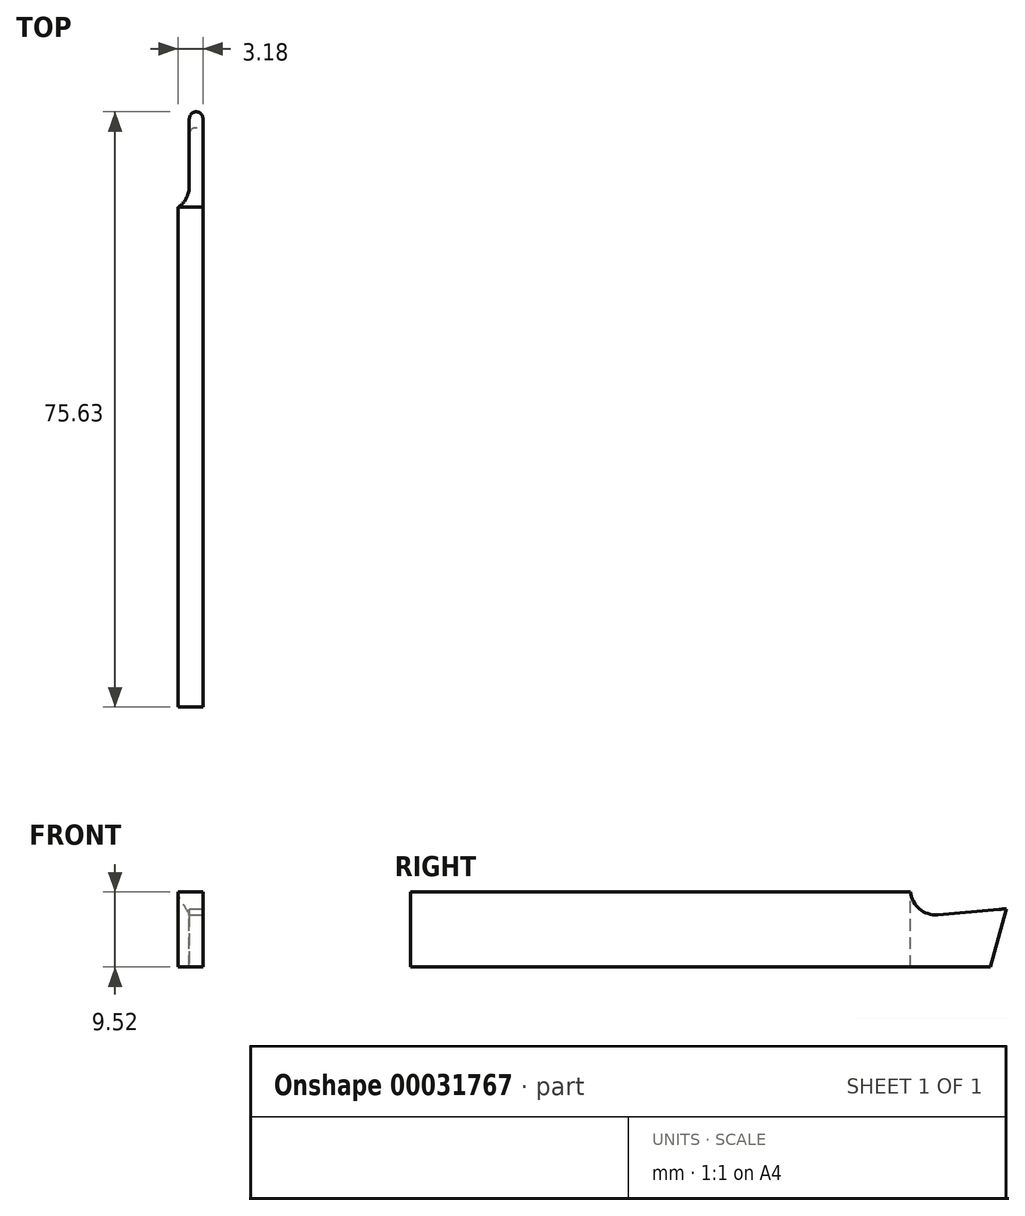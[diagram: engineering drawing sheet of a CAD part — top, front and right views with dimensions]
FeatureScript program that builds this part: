
annotation { "Feature Type Name" : "Feature", "Feature Type Description" : "" }
export const myFeature = defineFeature(function(context is Context, id is Id, definition is map)
    precondition{}
    {
        {
            var Q0;
            Q0=qCreatedBy(makeId("Right.planeOp"),FACE);
            var sketch = newSketch(context, id + "F3", { "sketchPlane" : qUnion([Q0])});
            skLineSegment(sketch, "E0.rect.bottom", {"start": v(38.1, 4.76) * mm, "end": v(-38.1, 4.76) * mm});
            skLineSegment(sketch, "E0.rect.top", {"start": v(38.1, -4.76) * mm, "end": v(-38.1, -4.76) * mm});
            skLineSegment(sketch, "E0.rect.left", {"start": v(38.1, 4.76) * mm, "end": v(38.1, -4.76) * mm});
            skLineSegment(sketch, "E0.rect.right", {"start": v(-38.1, 4.76) * mm, "end": v(-38.1, -4.76) * mm});
            skPoint(sketch, "E0.rect.middle", {"position": v(0, 0) * mm});
            skLineSegment(sketch, "E1", {"start": v(38.1, 4.76) * mm, "end": v(35.55, -4.76) * mm});
            skSolve(sketch);
        }
        {
            var Q0;
            Q0=makeQuery(id+"F3.imprint","IMPRINT",FACE,{"disambiguationData":[TD([[makeQuery(id+"F3.imprint","IMPRINT",EDGE,{"derivedFrom":sQuery(id+"F3.wireOp",EDGE,"E0.rect.bottom")}),1.0]])]});
            extrude(context, id + "F4", {"entities" : qUnion([Q0]), "endBound" : BoundingType.SYMMETRIC, "depth" : 3.17 * mm});
        }
        {
            var Q0;
            Q0=makeQuery(id+"F4.opExtrude","SWEPT_FACE",FACE,{"disambiguationData":[OSD([sQuery(id+"F3.wireOp",EDGE,"E0.rect.bottom")])]});
            var sketch = newSketch(context, id + "F0", { "sketchPlane" : qUnion([Q0])});
            skLineSegment(sketch, "E2.bottom", {"start": v(-1.59, 38.1) * mm, "end": v(-0.17, 38.1) * mm});
            skLineSegment(sketch, "E2.top", {"start": v(-1.59, 25.4) * mm, "end": v(-0.17, 25.4) * mm});
            skLineSegment(sketch, "E2.left", {"start": v(-1.59, 38.1) * mm, "end": v(-1.59, 25.4) * mm});
            skLineSegment(sketch, "E2.right", {"start": v(-0.17, 38.1) * mm, "end": v(-0.17, 25.4) * mm});
            skSolve(sketch);
        }
        {
            var Q0;
            Q0 = qSketchRegion(id + "F0", true);
            extrude(context, id + "F5", {"entities" : qUnion([Q0]), "operationType" : NewBodyOperationType.REMOVE, "oppositeDirection" : true, "depth" : 25.4 * mm});
        }
        {
            var Q0;
            Q0=makeQuery(id+"F4.opExtrude","CAP_EDGE",EDGE,{"disambiguationData":[OSD([sQuery(id+"F3.wireOp",EDGE,"E1")])],"isStart":false});
            var Q1;
            Q1=makeQuery(id+"F5.boolean.opBoolean","INTERSECT",EDGE,{"derivedFrom":[makeQuery(id+"F4.opExtrude","SWEPT_FACE",FACE,{"disambiguationData":[OSD([sQuery(id+"F3.wireOp",EDGE,"E1")])]}),makeQuery(id+"F5.opExtrude","SWEPT_FACE",FACE,{"disambiguationData":[OSD([sQuery(id+"F0.wireOp",EDGE,"E2.right")])]})]});
            fillet(context, id + "F1", {"entities" : qUnion([Q0, Q1]), "radius" : 0.88 * mm, "tangentPropagation" : true, "allowEdgeOverflow" : false});
        }
        {
            var Q0;
            Q0=makeQuery(id+"F4.opExtrude","CAP_FACE",FACE,{"disambiguationData":[OSD([sQuery(id+"F3.wireOp",EDGE,"E0.rect.bottom"),sQuery(id+"F3.wireOp",EDGE,"E0.rect.top"),sQuery(id+"F3.wireOp",EDGE,"E0.rect.right"),sQuery(id+"F3.wireOp",EDGE,"E1")])],"isStart":false});
            var sketch = newSketch(context, id + "F6", { "sketchPlane" : qUnion([Q0])});
            skLineSegment(sketch, "E3", {"start": v(25.4, 4.76) * mm, "end": v(43.7, 4.76) * mm});
            skLineSegment(sketch, "E4", {"start": v(43.7, 4.76) * mm, "end": v(43.7, 3.19) * mm});
            skLineSegment(sketch, "E5", {"start": v(25.4, 4.76) * mm, "end": v(25.4, 1.59) * mm});
            skLineSegment(sketch, "E6", {"start": v(25.4, 1.59) * mm, "end": v(43.7, 3.19) * mm});
            skSolve(sketch);
        }
        {
            var Q0;
            {var subQ7=sQuery(id+"F6.wireOp",EDGE,"E5");Q0=makeQuery(id+"F6.imprint","IMPRINT",FACE,{"disambiguationData":[TD([[makeQuery(id+"F6.imprint","IMPRINT",EDGE,{"derivedFrom":subQ7}),1.0]])]});}
            var Q1;
            {var subQ6=sQuery(id+"F6.wireOp",EDGE,"E4");Q1=makeQuery(id+"F6.imprint","IMPRINT",FACE,{"disambiguationData":[TD([[makeQuery(id+"F6.imprint","IMPRINT",EDGE,{"derivedFrom":subQ6}),-1.0]])]});}
            extrude(context, id + "F2", {"entities" : qUnion([Q0, Q1]), "operationType" : NewBodyOperationType.REMOVE, "oppositeDirection" : true, "depth" : 25.4 * mm});
        }
        {
            var Q0;
            Q0=makeQuery(id+"F2.boolean.opBoolean","COPY",EDGE,{"derivedFrom":makeQuery(id+"F2.opExtrude","SWEPT_EDGE",EDGE,{"disambiguationData":[OSD([sQuery(id+"F6.wireOp",EDGE,"E5"),sQuery(id+"F6.wireOp",EDGE,"E6")])]})});
            var Q1;
            Q1=makeQuery(id+"F5.boolean.opBoolean","COPY",EDGE,{"derivedFrom":makeQuery(id+"F5.opExtrude","SWEPT_EDGE",EDGE,{"disambiguationData":[OSD([sQuery(id+"F0.wireOp",EDGE,"E2.top"),sQuery(id+"F0.wireOp",EDGE,"E2.right")])]})});
            fillet(context, id + "F7", {"entities" : qUnion([Q0, Q1]), "radius" : 3.17 * mm, "tangentPropagation" : true, "allowEdgeOverflow" : false});
        }
    });
